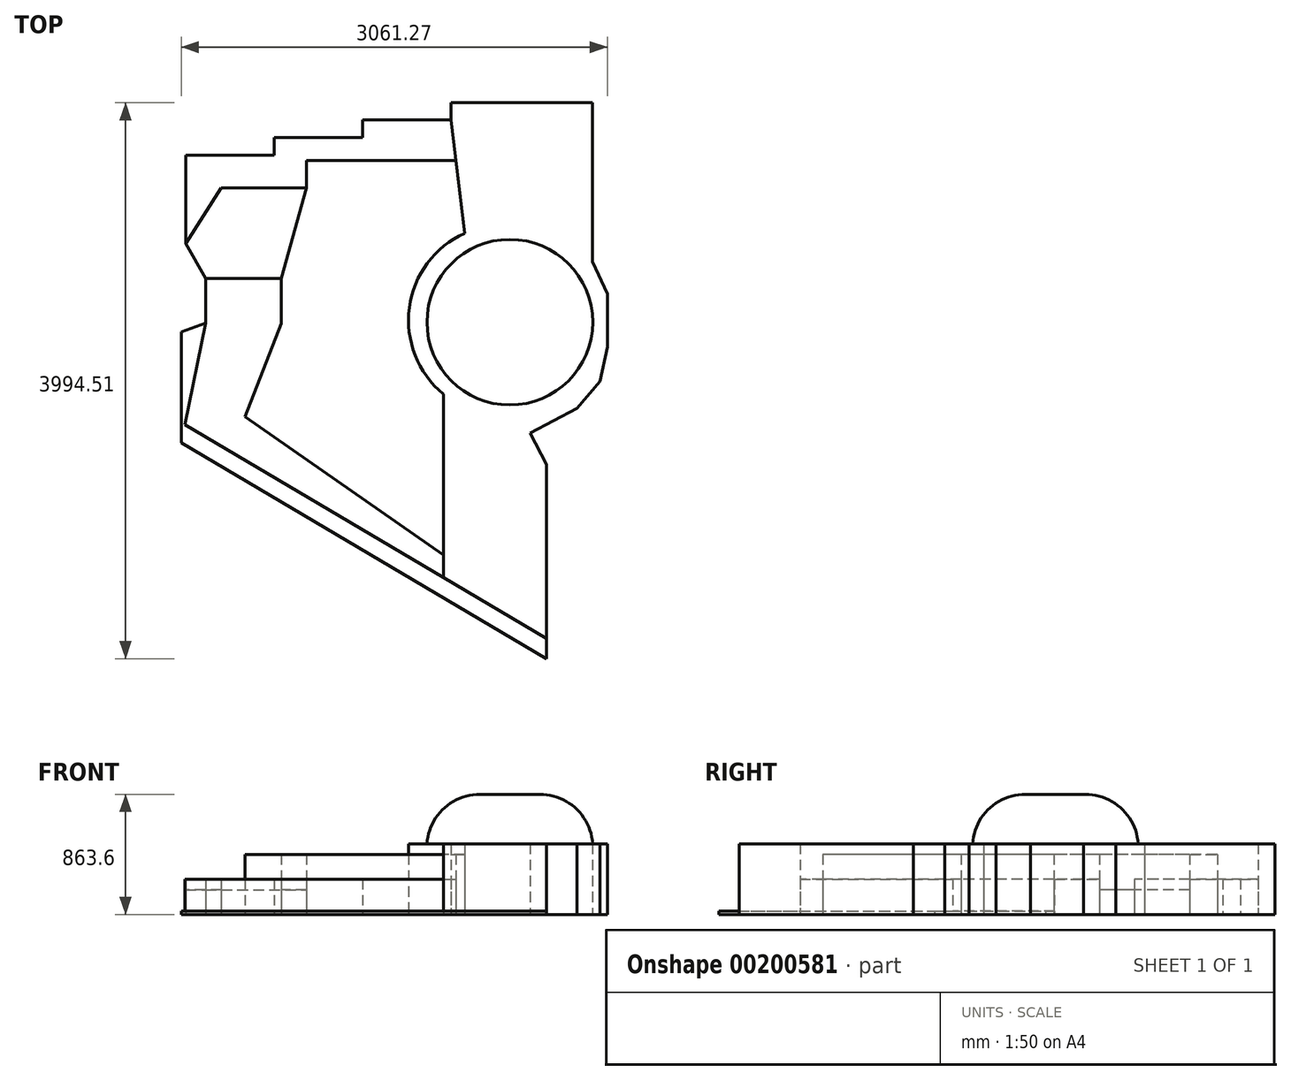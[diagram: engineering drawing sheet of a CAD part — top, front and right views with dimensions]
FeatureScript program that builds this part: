
annotation { "Feature Type Name" : "Feature", "Feature Type Description" : "" }
export const myFeature = defineFeature(function(context is Context, id is Id, definition is map)
    precondition{}
    {
        {
            var Q0;
            Q0=qCreatedBy(makeId("Top.planeOp"),FACE);
            var sketch = newSketch(context, id + "F0", { "sketchPlane" : qUnion([Q0])});
            skLineSegment(sketch, "E0", {"start": v(-351.9, 38.07) * mm, "end": v(283.1, 38.07) * mm});
            skLineSegment(sketch, "E1", {"start": v(283.1, 38.07) * mm, "end": v(283.1, 165.07) * mm});
            skLineSegment(sketch, "E2", {"start": v(283.1, 165.07) * mm, "end": v(918.1, 165.07) * mm});
            skLineSegment(sketch, "E3", {"start": v(918.1, 165.07) * mm, "end": v(918.1, 292.07) * mm});
            skLineSegment(sketch, "E4", {"start": v(918.1, 292.07) * mm, "end": v(1553.1, 292.07) * mm});
            skLineSegment(sketch, "E5", {"start": v(1553.1, 292.07) * mm, "end": v(1553.1, 413.42) * mm});
            skLineSegment(sketch, "E6", {"start": v(1553.1, 413.42) * mm, "end": v(2569.1, 413.42) * mm});
            skLineSegment(sketch, "E7", {"start": v(2569.1, 413.42) * mm, "end": v(2569.1, -729.58) * mm});
            skLineSegment(sketch, "E8", {"start": v(-351.9, 38.07) * mm, "end": v(-351.9, -596.93) * mm});
            skLineSegment(sketch, "E9", {"start": v(2569.1, -729.58) * mm, "end": v(2677.3, -959.39) * mm});
            skLineSegment(sketch, "E10", {"start": v(2677.3, -959.39) * mm, "end": v(2677.3, -1340.39) * mm});
            skLineSegment(sketch, "E11", {"start": v(2677.3, -1340.39) * mm, "end": v(2624.24, -1588.78) * mm});
            skLineSegment(sketch, "E12", {"start": v(2624.24, -1588.78) * mm, "end": v(2460.52, -1782.98) * mm});
            skLineSegment(sketch, "E13", {"start": v(2460.52, -1782.98) * mm, "end": v(2122.48, -1958.72) * mm});
            skLineSegment(sketch, "E14", {"start": v(2122.48, -1958.72) * mm, "end": v(2239.64, -2184.09) * mm});
            skLineSegment(sketch, "E15", {"start": v(2239.64, -2184.09) * mm, "end": v(2239.64, -3581.09) * mm});
            skLineSegment(sketch, "E16", {"start": v(2239.64, -3581.09) * mm, "end": v(-383.98, -2029.66) * mm});
            skLineSegment(sketch, "E17", {"start": v(-383.98, -2029.66) * mm, "end": v(-383.98, -1233.32) * mm});
            skLineSegment(sketch, "E18", {"start": v(-383.98, -1233.32) * mm, "end": v(-208.1, -1169.06) * mm});
            skLineSegment(sketch, "E19", {"start": v(-208.1, -1169.06) * mm, "end": v(-208.1, -847.77) * mm});
            skLineSegment(sketch, "E20", {"start": v(-351.9, -596.93) * mm, "end": v(-208.1, -847.77) * mm});
            skCircle(sketch, "E21", {"center": v(1976.7, -1163.56) * mm, "radius": 595 * mm});
            skArc(sketch, "E22", {"start": v(1651.92, -523.57) * mm, "mid": v(1254.66, -1059.04) * mm, "end": v(1499.09, -1679.37) * mm});
            skLineSegment(sketch, "E23", {"start": v(1553.1, 292.07) * mm, "end": v(1651.92, -523.57) * mm});
            skLineSegment(sketch, "E24", {"start": v(1499.09, -1679.37) * mm, "end": v(1499.09, -3143.18) * mm});
            skLineSegment(sketch, "E25", {"start": v(-208.1, -1169.06) * mm, "end": v(-383.98, -2029.66) * mm});
            skLineSegment(sketch, "E26", {"start": v(-96.11, -198.8) * mm, "end": v(-351.9, -596.93) * mm});
            skLineSegment(sketch, "E27", {"start": v(-208.1, -847.77) * mm, "end": v(333.73, -847.77) * mm});
            skLineSegment(sketch, "E28", {"start": v(333.73, -847.77) * mm, "end": v(333.73, -1173.11) * mm});
            skLineSegment(sketch, "E29", {"start": v(333.73, -1173.11) * mm, "end": v(75.82, -1841.76) * mm});
            skLineSegment(sketch, "E30", {"start": v(75.82, -1841.76) * mm, "end": v(1499.09, -2835.18) * mm});
            skLineSegment(sketch, "E31", {"start": v(-96.11, -198.8) * mm, "end": v(515.22, -198.8) * mm});
            skLineSegment(sketch, "E32", {"start": v(515.22, -198.8) * mm, "end": v(515.22, 0) * mm});
            skLineSegment(sketch, "E33", {"start": v(515.22, 0) * mm, "end": v(1588.49, 0) * mm});
            skLineSegment(sketch, "E34", {"start": v(515.22, -198.8) * mm, "end": v(333.73, -847.77) * mm});
            skLineSegment(sketch, "E35", {"start": v(2239.64, -3435.23) * mm, "end": v(-357.39, -1899.53) * mm});
            skSolve(sketch);
        }
        {
            var Q0;
            {var subQ0=sQuery(id+"F0.wireOp",EDGE,"E16");var subQ1=sQuery(id+"F0.wireOp",EDGE,"E15");var subQ2=makeQuery(id+"F0.imprint","INTERSECT",VERTEX,{"derivedFrom":[subQ1,subQ0]});Q0=makeQuery(id+"F0.imprint","IMPRINT",FACE,{"disambiguationData":[TD([[makeQuery(id+"F0.imprint","IMPRINT",EDGE,{"disambiguationData":[TD([[subQ2,1.0]])],"derivedFrom":subQ1}),-1.0]])]});}
            var Q1;
            {var subQ0=sQuery(id+"F0.wireOp",EDGE,"E17");Q1=makeQuery(id+"F0.imprint","IMPRINT",FACE,{"disambiguationData":[TD([[makeQuery(id+"F0.imprint","IMPRINT",EDGE,{"derivedFrom":subQ0}),-1.0]])]});}
            var Q2;
            {var subQ1=sQuery(id+"F0.wireOp",EDGE,"E16");var subQ3=sQuery(id+"F0.wireOp",EDGE,"E24");var subQ4=makeQuery(id+"F0.imprint","INTERSECT",VERTEX,{"derivedFrom":[subQ1,subQ3]});Q2=makeQuery(id+"F0.imprint","IMPRINT",FACE,{"disambiguationData":[TD([[makeQuery(id+"F0.imprint","IMPRINT",EDGE,{"disambiguationData":[TD([[subQ4,1.0]])],"derivedFrom":subQ3}),-1.0]])]});}
            extrude(context, id + "F1", {"entities" : qUnion([Q0, Q1, Q2]), "depth" : 25.4 * mm});
        }
        {
            var Q0;
            {var subQ1=sQuery(id+"F0.wireOp",EDGE,"E19");Q0=makeQuery(id+"F0.imprint","IMPRINT",FACE,{"disambiguationData":[TD([[makeQuery(id+"F0.imprint","IMPRINT",EDGE,{"derivedFrom":subQ1}),-1.0]])]});}
            var Q1;
            Q1=makeQuery(id+"F0.imprint","IMPRINT",FACE,{"disambiguationData":[TD([[makeQuery(id+"F0.imprint","IMPRINT",EDGE,{"derivedFrom":sQuery(id+"F0.wireOp",EDGE,"E0")}),-1.0]])]});
            extrude(context, id + "F2", {"entities" : qUnion([Q0, Q1]), "operationType" : NewBodyOperationType.ADD, "depth" : 254 * mm});
        }
        {
            var Q0;
            Q0=makeQuery(id+"F0.imprint","IMPRINT",FACE,{"disambiguationData":[TD([[makeQuery(id+"F0.imprint","IMPRINT",EDGE,{"derivedFrom":sQuery(id+"F0.wireOp",EDGE,"E20")}),1.0]])]});
            extrude(context, id + "F3", {"entities" : qUnion([Q0]), "depth" : 177.8 * mm});
        }
        {
            var Q0;
            {var subQ1=sQuery(id+"F0.wireOp",EDGE,"E22");Q0=makeQuery(id+"F0.imprint","IMPRINT",FACE,{"disambiguationData":[TD([[makeQuery(id+"F0.imprint","IMPRINT",EDGE,{"derivedFrom":subQ1}),-1.0]])]});}
            extrude(context, id + "F4", {"entities" : qUnion([Q0]), "depth" : 431.8 * mm});
        }
        {
            var Q0;
            {var subQ7=sQuery(id+"F0.wireOp",EDGE,"E5");Q0=makeQuery(id+"F0.imprint","IMPRINT",FACE,{"disambiguationData":[TD([[makeQuery(id+"F0.imprint","IMPRINT",EDGE,{"derivedFrom":subQ7}),-1.0]])]});}
            extrude(context, id + "F5", {"entities" : qUnion([Q0]), "depth" : 508 * mm});
        }
        {
            var Q0;
            Q0=makeQuery(id+"F0.imprint","IMPRINT",FACE,{"disambiguationData":[TD([[makeQuery(id+"F0.imprint","IMPRINT",EDGE,{"derivedFrom":sQuery(id+"F0.wireOp",EDGE,"E21")}),1.0]])]});
            extrude(context, id + "F6", {"entities" : qUnion([Q0]), "operationType" : NewBodyOperationType.ADD, "depth" : 863.6 * mm});
        }
        {
            var Q0;
            Q0=makeQuery(id+"F6.opExtrude","CAP_EDGE",EDGE,{"disambiguationData":[OSD([sQuery(id+"F0.wireOp",EDGE,"E21")])],"isStart":false});
            fillet(context, id + "F7", {"entities" : qUnion([Q0]), "radius" : 381 * mm, "tangentPropagation" : true, "allowEdgeOverflow" : false});
        }
    });
